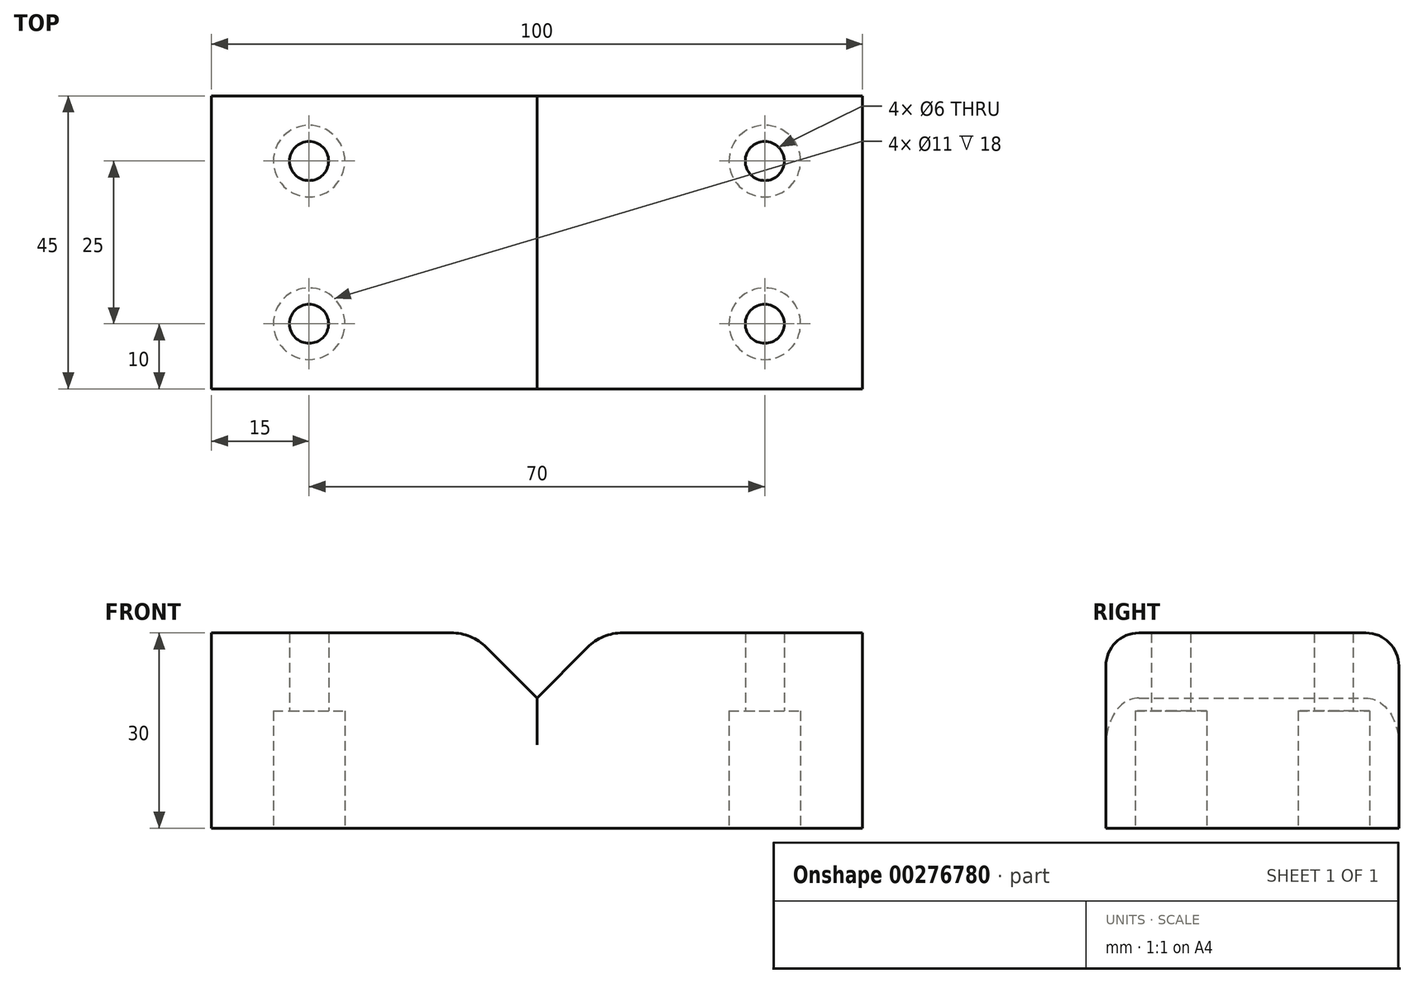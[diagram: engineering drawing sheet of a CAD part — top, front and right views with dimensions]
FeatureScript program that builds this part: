
annotation { "Feature Type Name" : "Feature", "Feature Type Description" : "" }
export const myFeature = defineFeature(function(context is Context, id is Id, definition is map)
    precondition{}
    {
        {
            var Q0;
            Q0=qCreatedBy(makeId("Front.planeOp"),FACE);
            var sketch = newSketch(context, id + "F0", { "sketchPlane" : qUnion([Q0])});
            skPoint(sketch, "E0.middle", {"position": v(0, 0) * mm});
            skLineSegment(sketch, "E1", {"start": v(20, 20) * mm, "end": v(50, 20) * mm});
            skLineSegment(sketch, "E2", {"start": v(50, 20) * mm, "end": v(50, 0) * mm});
            skLineSegment(sketch, "E3", {"start": v(-20, 20) * mm, "end": v(-50, 20) * mm});
            skLineSegment(sketch, "E4", {"start": v(-50, 20) * mm, "end": v(-50, 0) * mm});
            skLineSegment(sketch, "E5", {"start": v(-50, 0) * mm, "end": v(-50, -10) * mm});
            skLineSegment(sketch, "E6", {"start": v(-50, -10) * mm, "end": v(50, -10) * mm});
            skLineSegment(sketch, "E7", {"start": v(50, -10) * mm, "end": v(50, 0) * mm});
            skLineSegment(sketch, "E8", {"start": v(-20, 20) * mm, "end": v(-10, 20) * mm});
            skLineSegment(sketch, "E9", {"start": v(20, 20) * mm, "end": v(10, 20) * mm});
            skLineSegment(sketch, "E10", {"start": v(-10, 20) * mm, "end": v(0, 10) * mm});
            skLineSegment(sketch, "E11", {"start": v(0, 10) * mm, "end": v(10, 20) * mm});
            skSolve(sketch);
        }
        {
            var Q0;
            Q0=qSketchRegion(id+"F0",true);
            extrude(context, id + "F1", {"entities" : qUnion([Q0]), "depth" : 45 * mm});
        }
        {
            var Q0;
            Q0=makeQuery(id+"F1.opExtrude","SWEPT_EDGE",EDGE,{"disambiguationData":[OSD([sQuery(id+"F0.wireOp",EDGE,"E9"),sQuery(id+"F0.wireOp",EDGE,"E11")])]});
            var Q1;
            Q1=makeQuery(id+"F1.opExtrude","SWEPT_EDGE",EDGE,{"disambiguationData":[OSD([sQuery(id+"F0.wireOp",EDGE,"E8"),sQuery(id+"F0.wireOp",EDGE,"E10")])]});
            fillet(context, id + "F2", {"entities" : qUnion([Q0, Q1]), "radius" : 7.62 * mm, "tangentPropagation" : true, "allowEdgeOverflow" : false});
        }
        {
            var Q0;
            Q0=makeQuery(id+"F1.opExtrude","CAP_EDGE",EDGE,{"disambiguationData":[OSD([sQuery(id+"F0.wireOp",EDGE,"E3"),sQuery(id+"F0.wireOp",EDGE,"E8")])],"isStart":false});
            var Q1;
            Q1=makeQuery(id+"F1.opExtrude","CAP_EDGE",EDGE,{"disambiguationData":[OSD([sQuery(id+"F0.wireOp",EDGE,"E1"),sQuery(id+"F0.wireOp",EDGE,"E9")])],"isStart":false});
            var Q2;
            Q2=makeQuery(id+"F1.opExtrude","CAP_EDGE",EDGE,{"disambiguationData":[OSD([sQuery(id+"F0.wireOp",EDGE,"E1"),sQuery(id+"F0.wireOp",EDGE,"E9")])],"isStart":true});
            var Q3;
            Q3=makeQuery(id+"F1.opExtrude","CAP_EDGE",EDGE,{"disambiguationData":[OSD([sQuery(id+"F0.wireOp",EDGE,"E3"),sQuery(id+"F0.wireOp",EDGE,"E8")])],"isStart":true});
            fillet(context, id + "F3", {"entities" : qUnion([Q0, Q1, Q2, Q3]), "radius" : 5.08 * mm, "tangentPropagation" : true, "allowEdgeOverflow" : false});
        }
        {
            var Q0;
            Q0=makeQuery(id+"F1.opExtrude","SWEPT_FACE",FACE,{"disambiguationData":[OSD([sQuery(id+"F0.wireOp",EDGE,"E6")])]});
            var sketch = newSketch(context, id + "F4", { "sketchPlane" : qUnion([Q0])});
            skCircle(sketch, "E12", {"center": v(35, 35) * mm, "radius": 3 * mm});
            skCircle(sketch, "E13", {"center": v(35, 10) * mm, "radius": 3 * mm});
            skCircle(sketch, "E14", {"center": v(-35, 10) * mm, "radius": 3 * mm});
            skCircle(sketch, "E15", {"center": v(-35, 35) * mm, "radius": 3 * mm});
            skSolve(sketch);
        }
        {
            var Q0;
            Q0=sQuery(id+"F4.wireOp",VERTEX,"E13.center");
            var Q1;
            Q1=sQuery(id+"F4.wireOp",VERTEX,"E12.center");
            var Q2;
            Q2=sQuery(id+"F4.wireOp",VERTEX,"E15.center");
            var Q3;
            Q3=sQuery(id+"F4.wireOp",VERTEX,"E14.center");
            var Q4;
            Q4=makeQuery(id+"F1.opExtrude","SWEPT_BODY",BODY,{"disambiguationData":[OSD([sQuery(id+"F0.wireOp",EDGE,"E1"),sQuery(id+"F0.wireOp",EDGE,"E2"),sQuery(id+"F0.wireOp",EDGE,"E3"),sQuery(id+"F0.wireOp",EDGE,"E4"),sQuery(id+"F0.wireOp",EDGE,"E5"),sQuery(id+"F0.wireOp",EDGE,"E6"),sQuery(id+"F0.wireOp",EDGE,"E7"),sQuery(id+"F0.wireOp",EDGE,"E8"),sQuery(id+"F0.wireOp",EDGE,"E9"),sQuery(id+"F0.wireOp",EDGE,"E10"),sQuery(id+"F0.wireOp",EDGE,"E11")])]});
            hole(context, id + "F5", {"style" : HoleStyle.C_BORE, "endStyle" : HoleEndStyle.THROUGH, "holeDiameter" : 6 * mm, "cBoreDiameter" : 11 * mm, "cBoreDepth" : 18 * mm, "tappedDepth" : 12.7 * mm, "tapClearance" : 3, "locations" : qUnion([Q0, Q1, Q2, Q3]), "scope" : qUnion([Q4])});
        }
    });
